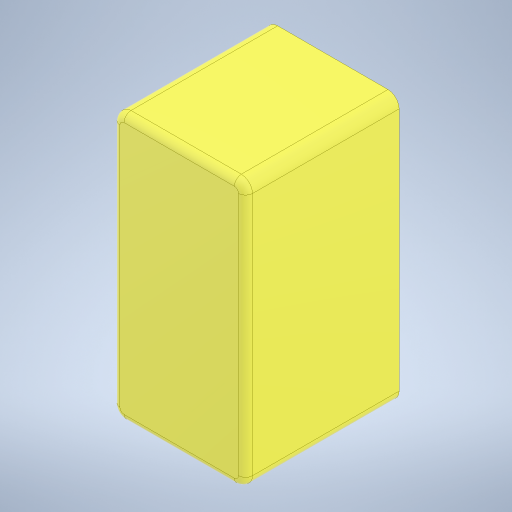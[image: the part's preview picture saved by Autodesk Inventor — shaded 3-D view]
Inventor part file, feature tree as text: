
AUTODESK INVENTOR PART (.ipt)
format: ipt  version: 2024 (Build 280153000, 153)  size: 296,960 bytes
history: native  units: mm
features: sketch x9, extrude x7, fillet x2, hole x2, other x1
ambient origin geometry x8: Origin, YZ Plane, XZ Plane, XY Plane, X Axis, Y Axis, Z Axis, Center Point
bodies: Body1 (feature_tree)
feature tree (21):
  other  "Těleso1"
  extrude  "Vysunutí1"  Depth=191.0mm
  extrude  "Vysunutí2"  Depth=95.0mm
  extrude  "Vysunutí3"  Depth=110.0mm TaperAngle=0.0deg
  extrude  "Vysunutí4"  Depth=85.0mm
  extrude  "Vysunutí6"  Depth=47.5mm
  fillet  "Zaoblení1"  Radius=85.0mm
  fillet  "Zaoblení2"  Radius=30.0mm
  extrude  "Vysunutí7"  Depth=85.0mm
  extrude  "Vysunutí8"  Depth=47.5mm
  hole  "Díra1"  [1 undecoded]
  hole  "Díra2"  [1 undecoded]
  sketch  "Náčrt1"
  sketch  "Náčrt2"
  sketch  "Náčrt3"
  sketch  "Náčrt4"
  sketch  "Náčrt6"
  sketch  "Náčrt7"
  sketch  "Náčrt8"
  sketch  "Náčrt9"
  sketch  "Náčrt10"
note: 2 required parameter values undecoded (feature->parameter linkage not recoverable at this tier; creation-order binding heuristic only, values carry confidence <= 0.55)
